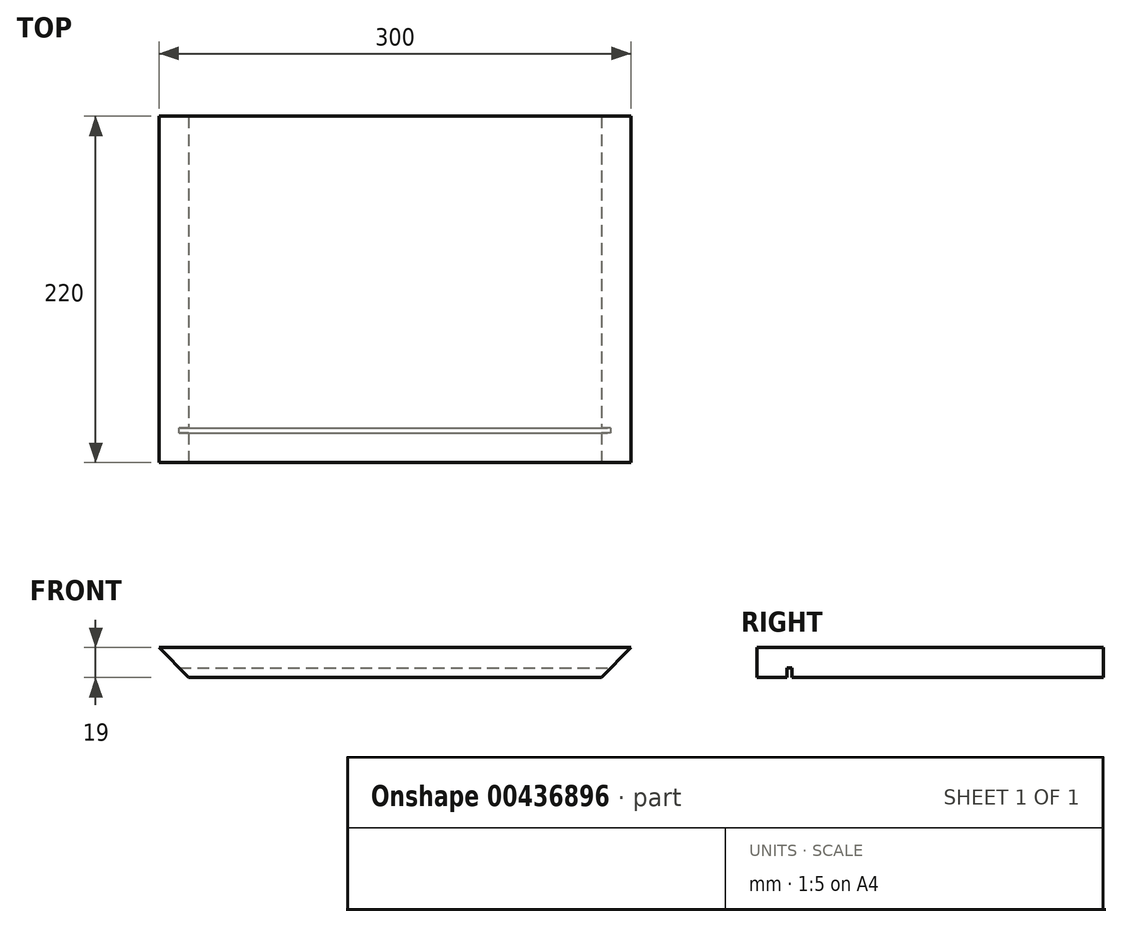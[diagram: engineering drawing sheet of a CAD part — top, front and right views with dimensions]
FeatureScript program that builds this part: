
annotation { "Feature Type Name" : "Feature", "Feature Type Description" : "" }
export const myFeature = defineFeature(function(context is Context, id is Id, definition is map)
    precondition{}
    {
        {
            var Q0;
            Q0=qCreatedBy(makeId("Front.planeOp"),FACE);
            var sketch = newSketch(context, id + "F0", { "sketchPlane" : qUnion([Q0])});
            skLineSegment(sketch, "E0", {"start": v(0, 0) * mm, "end": v(300, 0) * mm});
            skLineSegment(sketch, "E1", {"start": v(300, 0) * mm, "end": v(281, -19) * mm});
            skLineSegment(sketch, "E2", {"start": v(281, -19) * mm, "end": v(19, -19) * mm});
            skLineSegment(sketch, "E3", {"start": v(19, -19) * mm, "end": v(0, 0) * mm});
            skSolve(sketch);
        }
        {
            var Q0;
            Q0 = qSketchRegion(id + "F0", true);
            extrude(context, id + "F1", {"entities" : qUnion([Q0]), "oppositeDirection" : true, "depth" : 220 * mm});
        }
        {
            var Q0;
            Q0=makeQuery(id+"F1.opExtrude","SWEPT_FACE",FACE,{"disambiguationData":[OSD([sQuery(id+"F0.wireOp",EDGE,"E2")])]});
            var sketch = newSketch(context, id + "F2", { "sketchPlane" : qUnion([Q0])});
            skLineSegment(sketch, "E4.bottom", {"start": v(-7.05, -19) * mm, "end": v(351.23, -19) * mm});
            skLineSegment(sketch, "E4.top", {"start": v(-7.05, -22) * mm, "end": v(351.23, -22) * mm});
            skLineSegment(sketch, "E4.left", {"start": v(-7.05, -19) * mm, "end": v(-7.05, -22) * mm});
            skLineSegment(sketch, "E4.right", {"start": v(351.23, -19) * mm, "end": v(351.23, -22) * mm});
            skSolve(sketch);
        }
        {
            var Q0;
            Q0 = qSketchRegion(id + "F2", true);
            extrude(context, id + "F3", {"entities" : qUnion([Q0]), "operationType" : NewBodyOperationType.REMOVE, "oppositeDirection" : true, "depth" : 6 * mm});
        }
    });
